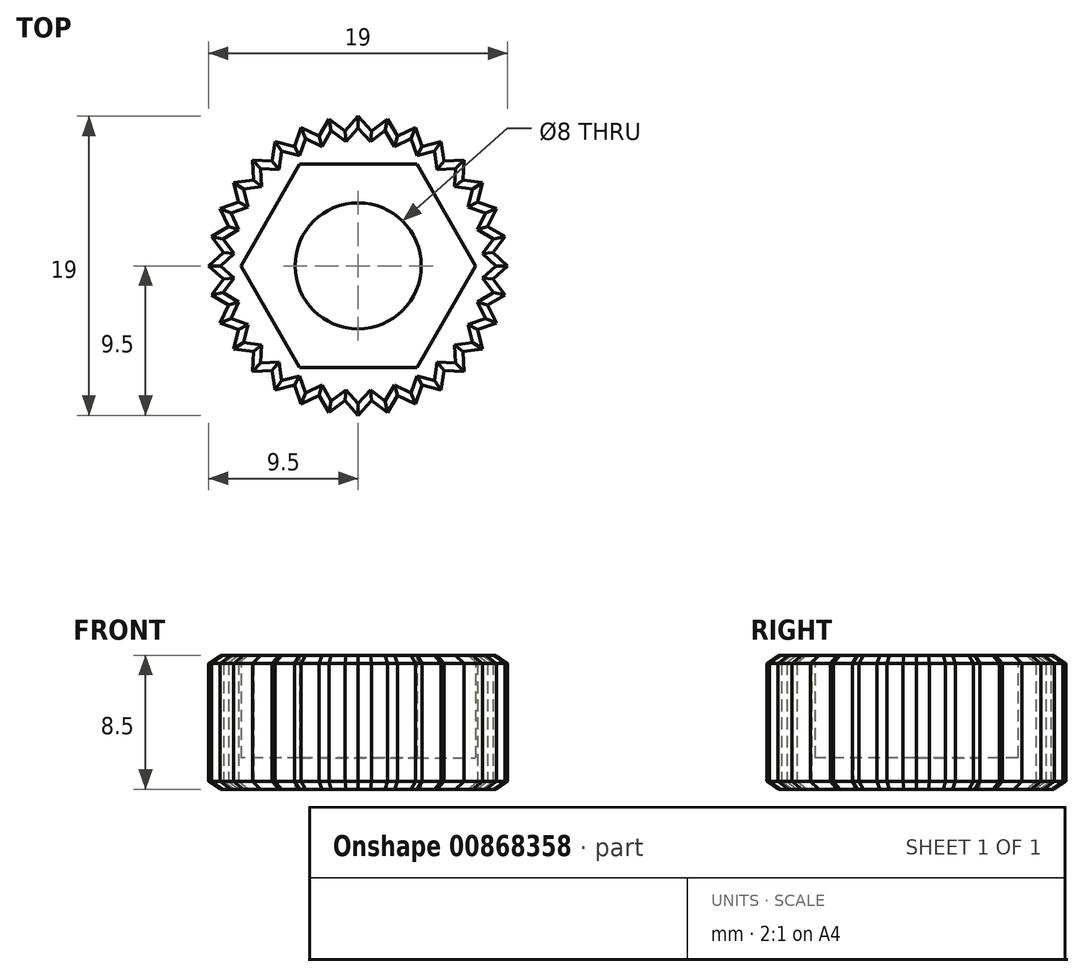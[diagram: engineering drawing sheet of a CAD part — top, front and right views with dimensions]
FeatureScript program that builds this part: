
annotation { "Feature Type Name" : "Feature", "Feature Type Description" : "" }
export const myFeature = defineFeature(function(context is Context, id is Id, definition is map)
    precondition{}
    {
        {
            var Q0;
            Q0=qCreatedBy(makeId("Top.planeOp"),FACE);
            var sketch = newSketch(context, id + "F0", { "sketchPlane" : qUnion([Q0])});
            skArc(sketch, "E0.cCircle", {"start": v(0, 6.45) * mm, "mid": v(-4.56, 4.56) * mm, "end": v(-6.45, 0) * mm, "construction": true});
            skLineSegment(sketch, "E0.4", {"start": v(-7.45, 0) * mm, "end": v(-3.72, 6.45) * mm});
            skLineSegment(sketch, "E0.5", {"start": v(-3.72, 6.45) * mm, "end": v(0, 6.45) * mm});
            skLineSegment(sketch, "E1", {"start": v(0, 12.28) * mm, "end": v(0, -11.98) * mm});
            skPoint(sketch, "E2", {"position": v(0, 9.5) * mm});
            skPoint(sketch, "E3", {"position": v(-9.5, 0) * mm});
            skCircle(sketch, "E4", {"center": v(0, 0) * mm, "radius": 8.6 * mm});
            skLineSegment(sketch, "E5", {"start": v(0, 9.5) * mm, "end": v(-0.84, 8.56) * mm});
            skLineSegment(sketch, "E6", {"start": v(-0.84, 8.56) * mm, "end": v(-1.85, 9.32) * mm});
            skLineSegment(sketch, "E7", {"start": v(-1.85, 9.32) * mm, "end": v(-2.5, 8.23) * mm});
            skLineSegment(sketch, "E8", {"start": v(-2.5, 8.23) * mm, "end": v(-3.64, 8.78) * mm});
            skLineSegment(sketch, "E9", {"start": v(-3.64, 8.78) * mm, "end": v(-4.05, 7.59) * mm});
            skLineSegment(sketch, "E10", {"start": v(-4.05, 7.59) * mm, "end": v(-5.28, 7.9) * mm});
            skLineSegment(sketch, "E11", {"start": v(-5.28, 7.9) * mm, "end": v(-5.46, 6.65) * mm});
            skLineSegment(sketch, "E12", {"start": v(-5.46, 6.65) * mm, "end": v(-6.72, 6.72) * mm});
            skLineSegment(sketch, "E13", {"start": v(-6.72, 6.72) * mm, "end": v(-6.65, 5.46) * mm});
            skLineSegment(sketch, "E14", {"start": v(-6.65, 5.46) * mm, "end": v(-7.9, 5.28) * mm});
            skLineSegment(sketch, "E15", {"start": v(-7.9, 5.28) * mm, "end": v(-7.58, 4.05) * mm});
            skLineSegment(sketch, "E16", {"start": v(-7.58, 4.05) * mm, "end": v(-8.78, 3.64) * mm});
            skLineSegment(sketch, "E17", {"start": v(-8.78, 3.64) * mm, "end": v(-8.23, 2.5) * mm});
            skLineSegment(sketch, "E18", {"start": v(-8.23, 2.5) * mm, "end": v(-9.32, 1.85) * mm});
            skLineSegment(sketch, "E19", {"start": v(-9.32, 1.85) * mm, "end": v(-8.56, 0.84) * mm});
            skLineSegment(sketch, "E20", {"start": v(-8.56, 0.84) * mm, "end": v(-9.5, 0) * mm});
            skLineSegment(sketch, "E21.MirrorCS", {"start": v(6.65, 5.46) * mm, "end": v(7.9, 5.28) * mm});
            skLineSegment(sketch, "E22.MirrorCS", {"start": v(8.56, 0.84) * mm, "end": v(9.5, 0) * mm});
            skLineSegment(sketch, "E23.MirrorCS", {"start": v(3.64, 8.78) * mm, "end": v(4.05, 7.59) * mm});
            skArc(sketch, "E24.MirrorCS", {"start": v(0, 6.45) * mm, "mid": v(4.56, 4.56) * mm, "end": v(6.45, 0) * mm, "construction": true});
            skLineSegment(sketch, "E25.MirrorCS", {"start": v(7.58, 4.05) * mm, "end": v(8.78, 3.64) * mm});
            skLineSegment(sketch, "E26.MirrorCS", {"start": v(4.05, 7.59) * mm, "end": v(5.28, 7.9) * mm});
            skLineSegment(sketch, "E27.MirrorCS", {"start": v(0.84, 8.56) * mm, "end": v(1.85, 9.32) * mm});
            skLineSegment(sketch, "E28.MirrorCS", {"start": v(8.23, 2.5) * mm, "end": v(9.32, 1.85) * mm});
            skLineSegment(sketch, "E29.MirrorCS", {"start": v(1.85, 9.32) * mm, "end": v(2.5, 8.23) * mm});
            skLineSegment(sketch, "E30.MirrorCS", {"start": v(0, 9.5) * mm, "end": v(0.84, 8.56) * mm});
            skLineSegment(sketch, "E31.MirrorCS", {"start": v(8.78, 3.64) * mm, "end": v(8.23, 2.5) * mm});
            skLineSegment(sketch, "E32.MirrorCS", {"start": v(2.5, 8.23) * mm, "end": v(3.64, 8.78) * mm});
            skLineSegment(sketch, "E33.MirrorCS", {"start": v(9.32, 1.85) * mm, "end": v(8.56, 0.84) * mm});
            skLineSegment(sketch, "E34.MirrorCS", {"start": v(5.28, 7.9) * mm, "end": v(5.46, 6.65) * mm});
            skLineSegment(sketch, "E35.MirrorCS", {"start": v(5.46, 6.65) * mm, "end": v(6.72, 6.72) * mm});
            skLineSegment(sketch, "E36.MirrorCS", {"start": v(3.72, 6.45) * mm, "end": v(0, 6.45) * mm});
            skLineSegment(sketch, "E37.MirrorCS", {"start": v(6.72, 6.72) * mm, "end": v(6.65, 5.46) * mm});
            skPoint(sketch, "E38.MirrorP", {"position": v(9.5, 0) * mm});
            skLineSegment(sketch, "E39.MirrorCS", {"start": v(7.45, 0) * mm, "end": v(3.72, 6.45) * mm});
            skLineSegment(sketch, "E40.MirrorCS", {"start": v(7.9, 5.28) * mm, "end": v(7.58, 4.05) * mm});
            skPoint(sketch, "E41.MirrorP", {"position": v(0, -9.5) * mm});
            skLineSegment(sketch, "E42.MirrorCS", {"start": v(1.85, -9.32) * mm, "end": v(2.5, -8.23) * mm});
            skLineSegment(sketch, "E43.MirrorCS", {"start": v(9.32, -1.85) * mm, "end": v(8.56, -0.84) * mm});
            skLineSegment(sketch, "E44.MirrorCS", {"start": v(0, -9.5) * mm, "end": v(-0.84, -8.56) * mm});
            skLineSegment(sketch, "E45.MirrorCS", {"start": v(-8.78, -3.64) * mm, "end": v(-8.23, -2.5) * mm});
            skLineSegment(sketch, "E46.MirrorCS", {"start": v(0.84, -8.56) * mm, "end": v(1.85, -9.32) * mm});
            skLineSegment(sketch, "E47.MirrorCS", {"start": v(5.28, -7.9) * mm, "end": v(5.46, -6.65) * mm});
            skLineSegment(sketch, "E48.MirrorCS", {"start": v(6.72, -6.72) * mm, "end": v(6.65, -5.46) * mm});
            skLineSegment(sketch, "E49.MirrorCS", {"start": v(-6.65, -5.46) * mm, "end": v(-7.9, -5.28) * mm});
            skLineSegment(sketch, "E50.MirrorCS", {"start": v(3.64, -8.78) * mm, "end": v(4.05, -7.59) * mm});
            skLineSegment(sketch, "E51.MirrorCS", {"start": v(-9.32, -1.85) * mm, "end": v(-8.56, -0.84) * mm});
            skLineSegment(sketch, "E52.MirrorCS", {"start": v(-5.28, -7.9) * mm, "end": v(-5.46, -6.65) * mm});
            skLineSegment(sketch, "E53.MirrorCS", {"start": v(5.46, -6.65) * mm, "end": v(6.72, -6.72) * mm});
            skLineSegment(sketch, "E54.MirrorCS", {"start": v(-7.9, -5.28) * mm, "end": v(-7.58, -4.05) * mm});
            skLineSegment(sketch, "E55.MirrorCS", {"start": v(-0.84, -8.56) * mm, "end": v(-1.85, -9.32) * mm});
            skLineSegment(sketch, "E56.MirrorCS", {"start": v(8.78, -3.64) * mm, "end": v(8.23, -2.5) * mm});
            skLineSegment(sketch, "E57.MirrorCS", {"start": v(2.5, -8.23) * mm, "end": v(3.64, -8.78) * mm});
            skLineSegment(sketch, "E58.MirrorCS", {"start": v(-7.58, -4.05) * mm, "end": v(-8.78, -3.64) * mm});
            skLineSegment(sketch, "E59.MirrorCS", {"start": v(-3.72, -6.45) * mm, "end": v(0, -6.45) * mm});
            skLineSegment(sketch, "E60.MirrorCS", {"start": v(-3.64, -8.78) * mm, "end": v(-4.05, -7.59) * mm});
            skLineSegment(sketch, "E61.MirrorCS", {"start": v(-8.23, -2.5) * mm, "end": v(-9.32, -1.85) * mm});
            skLineSegment(sketch, "E62.MirrorCS", {"start": v(4.05, -7.59) * mm, "end": v(5.28, -7.9) * mm});
            skLineSegment(sketch, "E63.MirrorCS", {"start": v(-4.05, -7.59) * mm, "end": v(-5.28, -7.9) * mm});
            skLineSegment(sketch, "E64.MirrorCS", {"start": v(6.65, -5.46) * mm, "end": v(7.9, -5.28) * mm});
            skLineSegment(sketch, "E65.MirrorCS", {"start": v(3.72, -6.45) * mm, "end": v(0, -6.45) * mm});
            skLineSegment(sketch, "E66.MirrorCS", {"start": v(-1.85, -9.32) * mm, "end": v(-2.5, -8.23) * mm});
            skLineSegment(sketch, "E67.MirrorCS", {"start": v(0, -9.5) * mm, "end": v(0.84, -8.56) * mm});
            skLineSegment(sketch, "E68.MirrorCS", {"start": v(-6.72, -6.72) * mm, "end": v(-6.65, -5.46) * mm});
            skLineSegment(sketch, "E69.MirrorCS", {"start": v(7.58, -4.05) * mm, "end": v(8.78, -3.64) * mm});
            skLineSegment(sketch, "E70.MirrorCS", {"start": v(7.9, -5.28) * mm, "end": v(7.58, -4.05) * mm});
            skLineSegment(sketch, "E71.MirrorCS", {"start": v(-2.5, -8.23) * mm, "end": v(-3.64, -8.78) * mm});
            skLineSegment(sketch, "E72.MirrorCS", {"start": v(8.23, -2.5) * mm, "end": v(9.32, -1.85) * mm});
            skLineSegment(sketch, "E73.MirrorCS", {"start": v(-5.46, -6.65) * mm, "end": v(-6.72, -6.72) * mm});
            skLineSegment(sketch, "E74", {"start": v(-8.56, -0.84) * mm, "end": v(-9.5, 0) * mm});
            skLineSegment(sketch, "E75", {"start": v(8.56, -0.84) * mm, "end": v(9.5, 0) * mm});
            skLineSegment(sketch, "E76", {"start": v(-7.45, 0) * mm, "end": v(-3.72, -6.45) * mm});
            skLineSegment(sketch, "E77", {"start": v(3.72, -6.45) * mm, "end": v(7.45, 0) * mm});
            skSolve(sketch);
        }
        {
            var Q0;
            Q0=makeQuery(id+"F0.imprint","IMPRINT",FACE,{"disambiguationData":[TD([[makeQuery(id+"F0.imprint","IMPRINT",EDGE,{"derivedFrom":sQuery(id+"F0.wireOp",EDGE,"E0.4")}),1.0]])]});
            var Q1;
            {var subQ16=sQuery(id+"F0.wireOp",EDGE,"E36.MirrorCS");Q1=makeQuery(id+"F0.imprint","IMPRINT",FACE,{"disambiguationData":[TD([[makeQuery(id+"F0.imprint","IMPRINT",EDGE,{"derivedFrom":subQ16}),-1.0]])]});}
            var Q2;
            Q2=makeQuery(id+"F0.imprint","IMPRINT",FACE,{"disambiguationData":[TD([[makeQuery(id+"F0.imprint","IMPRINT",EDGE,{"derivedFrom":sQuery(id+"F0.wireOp",EDGE,"E0.4")}),-1.0]])]});
            var Q3;
            {var subQ1=sQuery(id+"F0.wireOp",EDGE,"E36.MirrorCS");Q3=makeQuery(id+"F0.imprint","IMPRINT",FACE,{"disambiguationData":[TD([[makeQuery(id+"F0.imprint","IMPRINT",EDGE,{"derivedFrom":subQ1}),1.0]])]});}
            var Q4;
            {var subQ0=sQuery(id+"F0.wireOp",EDGE,"E6");Q4=makeQuery(id+"F0.imprint","IMPRINT",FACE,{"disambiguationData":[TD([[makeQuery(id+"F0.imprint","IMPRINT",EDGE,{"derivedFrom":subQ0}),1.0]])]});}
            var Q5;
            {var subQ0=sQuery(id+"F0.wireOp",EDGE,"E8");Q5=makeQuery(id+"F0.imprint","IMPRINT",FACE,{"disambiguationData":[TD([[makeQuery(id+"F0.imprint","IMPRINT",EDGE,{"derivedFrom":subQ0}),1.0]])]});}
            var Q6;
            {var subQ0=sQuery(id+"F0.wireOp",EDGE,"E30.MirrorCS");Q6=makeQuery(id+"F0.imprint","IMPRINT",FACE,{"disambiguationData":[TD([[makeQuery(id+"F0.imprint","IMPRINT",EDGE,{"derivedFrom":subQ0}),-1.0]])]});}
            var Q7;
            {var subQ0=sQuery(id+"F0.wireOp",EDGE,"E25.MirrorCS");Q7=makeQuery(id+"F0.imprint","IMPRINT",FACE,{"disambiguationData":[TD([[makeQuery(id+"F0.imprint","IMPRINT",EDGE,{"derivedFrom":subQ0}),-1.0]])]});}
            var Q8;
            {var subQ0=sQuery(id+"F0.wireOp",EDGE,"E26.MirrorCS");Q8=makeQuery(id+"F0.imprint","IMPRINT",FACE,{"disambiguationData":[TD([[makeQuery(id+"F0.imprint","IMPRINT",EDGE,{"derivedFrom":subQ0}),-1.0]])]});}
            var Q9;
            {var subQ0=sQuery(id+"F0.wireOp",EDGE,"E64.MirrorCS");Q9=makeQuery(id+"F0.imprint","IMPRINT",FACE,{"disambiguationData":[TD([[makeQuery(id+"F0.imprint","IMPRINT",EDGE,{"derivedFrom":subQ0}),1.0]])]});}
            var Q10;
            {var subQ0=sQuery(id+"F0.wireOp",EDGE,"E5");Q10=makeQuery(id+"F0.imprint","IMPRINT",FACE,{"disambiguationData":[TD([[makeQuery(id+"F0.imprint","IMPRINT",EDGE,{"derivedFrom":subQ0}),1.0]])]});}
            var Q11;
            {var subQ0=sQuery(id+"F0.wireOp",EDGE,"E67.MirrorCS");Q11=makeQuery(id+"F0.imprint","IMPRINT",FACE,{"disambiguationData":[TD([[makeQuery(id+"F0.imprint","IMPRINT",EDGE,{"derivedFrom":subQ0}),1.0]])]});}
            var Q12;
            {var subQ0=sQuery(id+"F0.wireOp",EDGE,"E52.MirrorCS");Q12=makeQuery(id+"F0.imprint","IMPRINT",FACE,{"disambiguationData":[TD([[makeQuery(id+"F0.imprint","IMPRINT",EDGE,{"derivedFrom":subQ0}),-1.0]])]});}
            var Q13;
            {var subQ0=sQuery(id+"F0.wireOp",EDGE,"E10");Q13=makeQuery(id+"F0.imprint","IMPRINT",FACE,{"disambiguationData":[TD([[makeQuery(id+"F0.imprint","IMPRINT",EDGE,{"derivedFrom":subQ0}),1.0]])]});}
            var Q14;
            {var subQ2=sQuery(id+"F0.wireOp",EDGE,"E50.MirrorCS");Q14=makeQuery(id+"F0.imprint","IMPRINT",FACE,{"disambiguationData":[TD([[makeQuery(id+"F0.imprint","IMPRINT",EDGE,{"derivedFrom":subQ2}),1.0]])]});}
            var Q15;
            {var subQ0=sQuery(id+"F0.wireOp",EDGE,"E14");Q15=makeQuery(id+"F0.imprint","IMPRINT",FACE,{"disambiguationData":[TD([[makeQuery(id+"F0.imprint","IMPRINT",EDGE,{"derivedFrom":subQ0}),1.0]])]});}
            var Q16;
            {var subQ0=sQuery(id+"F0.wireOp",EDGE,"E18");Q16=makeQuery(id+"F0.imprint","IMPRINT",FACE,{"disambiguationData":[TD([[makeQuery(id+"F0.imprint","IMPRINT",EDGE,{"derivedFrom":subQ0}),1.0]])]});}
            var Q17;
            {var subQ0=sQuery(id+"F0.wireOp",EDGE,"E16");Q17=makeQuery(id+"F0.imprint","IMPRINT",FACE,{"disambiguationData":[TD([[makeQuery(id+"F0.imprint","IMPRINT",EDGE,{"derivedFrom":subQ0}),1.0]])]});}
            var Q18;
            {var subQ2=sQuery(id+"F0.wireOp",EDGE,"E51.MirrorCS");Q18=makeQuery(id+"F0.imprint","IMPRINT",FACE,{"disambiguationData":[TD([[makeQuery(id+"F0.imprint","IMPRINT",EDGE,{"derivedFrom":subQ2}),-1.0]])]});}
            var Q19;
            {var subQ0=sQuery(id+"F0.wireOp",EDGE,"E27.MirrorCS");Q19=makeQuery(id+"F0.imprint","IMPRINT",FACE,{"disambiguationData":[TD([[makeQuery(id+"F0.imprint","IMPRINT",EDGE,{"derivedFrom":subQ0}),-1.0]])]});}
            var Q20;
            {var subQ0=sQuery(id+"F0.wireOp",EDGE,"E42.MirrorCS");Q20=makeQuery(id+"F0.imprint","IMPRINT",FACE,{"disambiguationData":[TD([[makeQuery(id+"F0.imprint","IMPRINT",EDGE,{"derivedFrom":subQ0}),1.0]])]});}
            var Q21;
            {var subQ0=sQuery(id+"F0.wireOp",EDGE,"E20");Q21=makeQuery(id+"F0.imprint","IMPRINT",FACE,{"disambiguationData":[TD([[makeQuery(id+"F0.imprint","IMPRINT",EDGE,{"derivedFrom":subQ0}),1.0]])]});}
            var Q22;
            {var subQ0=sQuery(id+"F0.wireOp",EDGE,"E23.MirrorCS");Q22=makeQuery(id+"F0.imprint","IMPRINT",FACE,{"disambiguationData":[TD([[makeQuery(id+"F0.imprint","IMPRINT",EDGE,{"derivedFrom":subQ0}),-1.0]])]});}
            var Q23;
            {var subQ0=sQuery(id+"F0.wireOp",EDGE,"E49.MirrorCS");Q23=makeQuery(id+"F0.imprint","IMPRINT",FACE,{"disambiguationData":[TD([[makeQuery(id+"F0.imprint","IMPRINT",EDGE,{"derivedFrom":subQ0}),-1.0]])]});}
            var Q24;
            {var subQ0=sQuery(id+"F0.wireOp",EDGE,"E47.MirrorCS");Q24=makeQuery(id+"F0.imprint","IMPRINT",FACE,{"disambiguationData":[TD([[makeQuery(id+"F0.imprint","IMPRINT",EDGE,{"derivedFrom":subQ0}),1.0]])]});}
            var Q25;
            {var subQ0=sQuery(id+"F0.wireOp",EDGE,"E22.MirrorCS");Q25=makeQuery(id+"F0.imprint","IMPRINT",FACE,{"disambiguationData":[TD([[makeQuery(id+"F0.imprint","IMPRINT",EDGE,{"derivedFrom":subQ0}),-1.0]])]});}
            var Q26;
            {var subQ0=sQuery(id+"F0.wireOp",EDGE,"E28.MirrorCS");Q26=makeQuery(id+"F0.imprint","IMPRINT",FACE,{"disambiguationData":[TD([[makeQuery(id+"F0.imprint","IMPRINT",EDGE,{"derivedFrom":subQ0}),-1.0]])]});}
            var Q27;
            {var subQ0=sQuery(id+"F0.wireOp",EDGE,"E35.MirrorCS");Q27=makeQuery(id+"F0.imprint","IMPRINT",FACE,{"disambiguationData":[TD([[makeQuery(id+"F0.imprint","IMPRINT",EDGE,{"derivedFrom":subQ0}),-1.0]])]});}
            var Q28;
            {var subQ0=sQuery(id+"F0.wireOp",EDGE,"E43.MirrorCS");Q28=makeQuery(id+"F0.imprint","IMPRINT",FACE,{"disambiguationData":[TD([[makeQuery(id+"F0.imprint","IMPRINT",EDGE,{"derivedFrom":subQ0}),1.0]])]});}
            var Q29;
            {var subQ0=sQuery(id+"F0.wireOp",EDGE,"E68.MirrorCS");Q29=makeQuery(id+"F0.imprint","IMPRINT",FACE,{"disambiguationData":[TD([[makeQuery(id+"F0.imprint","IMPRINT",EDGE,{"derivedFrom":subQ0}),-1.0]])]});}
            var Q30;
            {var subQ0=sQuery(id+"F0.wireOp",EDGE,"E56.MirrorCS");Q30=makeQuery(id+"F0.imprint","IMPRINT",FACE,{"disambiguationData":[TD([[makeQuery(id+"F0.imprint","IMPRINT",EDGE,{"derivedFrom":subQ0}),1.0]])]});}
            var Q31;
            {var subQ0=sQuery(id+"F0.wireOp",EDGE,"E44.MirrorCS");Q31=makeQuery(id+"F0.imprint","IMPRINT",FACE,{"disambiguationData":[TD([[makeQuery(id+"F0.imprint","IMPRINT",EDGE,{"derivedFrom":subQ0}),-1.0]])]});}
            var Q32;
            {var subQ0=sQuery(id+"F0.wireOp",EDGE,"E45.MirrorCS");Q32=makeQuery(id+"F0.imprint","IMPRINT",FACE,{"disambiguationData":[TD([[makeQuery(id+"F0.imprint","IMPRINT",EDGE,{"derivedFrom":subQ0}),-1.0]])]});}
            var Q33;
            {var subQ0=sQuery(id+"F0.wireOp",EDGE,"E12");Q33=makeQuery(id+"F0.imprint","IMPRINT",FACE,{"disambiguationData":[TD([[makeQuery(id+"F0.imprint","IMPRINT",EDGE,{"derivedFrom":subQ0}),1.0]])]});}
            var Q34;
            {var subQ0=sQuery(id+"F0.wireOp",EDGE,"E60.MirrorCS");Q34=makeQuery(id+"F0.imprint","IMPRINT",FACE,{"disambiguationData":[TD([[makeQuery(id+"F0.imprint","IMPRINT",EDGE,{"derivedFrom":subQ0}),-1.0]])]});}
            var Q35;
            {var subQ0=sQuery(id+"F0.wireOp",EDGE,"E21.MirrorCS");Q35=makeQuery(id+"F0.imprint","IMPRINT",FACE,{"disambiguationData":[TD([[makeQuery(id+"F0.imprint","IMPRINT",EDGE,{"derivedFrom":subQ0}),-1.0]])]});}
            var Q36;
            {var subQ2=sQuery(id+"F0.wireOp",EDGE,"E48.MirrorCS");Q36=makeQuery(id+"F0.imprint","IMPRINT",FACE,{"disambiguationData":[TD([[makeQuery(id+"F0.imprint","IMPRINT",EDGE,{"derivedFrom":subQ2}),1.0]])]});}
            var Q37;
            {var subQ0=sQuery(id+"F0.wireOp",EDGE,"E55.MirrorCS");Q37=makeQuery(id+"F0.imprint","IMPRINT",FACE,{"disambiguationData":[TD([[makeQuery(id+"F0.imprint","IMPRINT",EDGE,{"derivedFrom":subQ0}),-1.0]])]});}
            extrude(context, id + "F1", {"entities" : qUnion([Q0, Q1, Q2, Q3, Q4, Q5, Q6, Q7, Q8, Q9, Q10, Q11, Q12, Q13, Q14, Q15, Q16, Q17, Q18, Q19, Q20, Q21, Q22, Q23, Q24, Q25, Q26, Q27, Q28, Q29, Q30, Q31, Q32, Q33, Q34, Q35, Q36, Q37]), "depth" : 2 * mm, "offsetDistance" : 25 * mm});
        }
        {
            var Q0;
            {var subQ16=sQuery(id+"F0.wireOp",EDGE,"E36.MirrorCS");Q0=makeQuery(id+"F0.imprint","IMPRINT",FACE,{"disambiguationData":[TD([[makeQuery(id+"F0.imprint","IMPRINT",EDGE,{"derivedFrom":subQ16}),-1.0]])]});}
            var Q1;
            Q1=makeQuery(id+"F0.imprint","IMPRINT",FACE,{"disambiguationData":[TD([[makeQuery(id+"F0.imprint","IMPRINT",EDGE,{"derivedFrom":sQuery(id+"F0.wireOp",EDGE,"E0.4")}),1.0]])]});
            var Q2;
            {var subQ0=sQuery(id+"F0.wireOp",EDGE,"E47.MirrorCS");Q2=makeQuery(id+"F0.imprint","IMPRINT",FACE,{"disambiguationData":[TD([[makeQuery(id+"F0.imprint","IMPRINT",EDGE,{"derivedFrom":subQ0}),1.0]])]});}
            var Q3;
            {var subQ2=sQuery(id+"F0.wireOp",EDGE,"E48.MirrorCS");Q3=makeQuery(id+"F0.imprint","IMPRINT",FACE,{"disambiguationData":[TD([[makeQuery(id+"F0.imprint","IMPRINT",EDGE,{"derivedFrom":subQ2}),1.0]])]});}
            var Q4;
            {var subQ0=sQuery(id+"F0.wireOp",EDGE,"E64.MirrorCS");Q4=makeQuery(id+"F0.imprint","IMPRINT",FACE,{"disambiguationData":[TD([[makeQuery(id+"F0.imprint","IMPRINT",EDGE,{"derivedFrom":subQ0}),1.0]])]});}
            var Q5;
            {var subQ0=sQuery(id+"F0.wireOp",EDGE,"E56.MirrorCS");Q5=makeQuery(id+"F0.imprint","IMPRINT",FACE,{"disambiguationData":[TD([[makeQuery(id+"F0.imprint","IMPRINT",EDGE,{"derivedFrom":subQ0}),1.0]])]});}
            var Q6;
            {var subQ0=sQuery(id+"F0.wireOp",EDGE,"E43.MirrorCS");Q6=makeQuery(id+"F0.imprint","IMPRINT",FACE,{"disambiguationData":[TD([[makeQuery(id+"F0.imprint","IMPRINT",EDGE,{"derivedFrom":subQ0}),1.0]])]});}
            var Q7;
            {var subQ0=sQuery(id+"F0.wireOp",EDGE,"E22.MirrorCS");Q7=makeQuery(id+"F0.imprint","IMPRINT",FACE,{"disambiguationData":[TD([[makeQuery(id+"F0.imprint","IMPRINT",EDGE,{"derivedFrom":subQ0}),-1.0]])]});}
            var Q8;
            {var subQ0=sQuery(id+"F0.wireOp",EDGE,"E28.MirrorCS");Q8=makeQuery(id+"F0.imprint","IMPRINT",FACE,{"disambiguationData":[TD([[makeQuery(id+"F0.imprint","IMPRINT",EDGE,{"derivedFrom":subQ0}),-1.0]])]});}
            var Q9;
            {var subQ0=sQuery(id+"F0.wireOp",EDGE,"E25.MirrorCS");Q9=makeQuery(id+"F0.imprint","IMPRINT",FACE,{"disambiguationData":[TD([[makeQuery(id+"F0.imprint","IMPRINT",EDGE,{"derivedFrom":subQ0}),-1.0]])]});}
            var Q10;
            {var subQ0=sQuery(id+"F0.wireOp",EDGE,"E21.MirrorCS");Q10=makeQuery(id+"F0.imprint","IMPRINT",FACE,{"disambiguationData":[TD([[makeQuery(id+"F0.imprint","IMPRINT",EDGE,{"derivedFrom":subQ0}),-1.0]])]});}
            var Q11;
            {var subQ0=sQuery(id+"F0.wireOp",EDGE,"E35.MirrorCS");Q11=makeQuery(id+"F0.imprint","IMPRINT",FACE,{"disambiguationData":[TD([[makeQuery(id+"F0.imprint","IMPRINT",EDGE,{"derivedFrom":subQ0}),-1.0]])]});}
            var Q12;
            {var subQ0=sQuery(id+"F0.wireOp",EDGE,"E26.MirrorCS");Q12=makeQuery(id+"F0.imprint","IMPRINT",FACE,{"disambiguationData":[TD([[makeQuery(id+"F0.imprint","IMPRINT",EDGE,{"derivedFrom":subQ0}),-1.0]])]});}
            var Q13;
            {var subQ0=sQuery(id+"F0.wireOp",EDGE,"E23.MirrorCS");Q13=makeQuery(id+"F0.imprint","IMPRINT",FACE,{"disambiguationData":[TD([[makeQuery(id+"F0.imprint","IMPRINT",EDGE,{"derivedFrom":subQ0}),-1.0]])]});}
            var Q14;
            {var subQ2=sQuery(id+"F0.wireOp",EDGE,"E50.MirrorCS");Q14=makeQuery(id+"F0.imprint","IMPRINT",FACE,{"disambiguationData":[TD([[makeQuery(id+"F0.imprint","IMPRINT",EDGE,{"derivedFrom":subQ2}),1.0]])]});}
            var Q15;
            {var subQ0=sQuery(id+"F0.wireOp",EDGE,"E42.MirrorCS");Q15=makeQuery(id+"F0.imprint","IMPRINT",FACE,{"disambiguationData":[TD([[makeQuery(id+"F0.imprint","IMPRINT",EDGE,{"derivedFrom":subQ0}),1.0]])]});}
            var Q16;
            {var subQ0=sQuery(id+"F0.wireOp",EDGE,"E67.MirrorCS");Q16=makeQuery(id+"F0.imprint","IMPRINT",FACE,{"disambiguationData":[TD([[makeQuery(id+"F0.imprint","IMPRINT",EDGE,{"derivedFrom":subQ0}),1.0]])]});}
            var Q17;
            {var subQ0=sQuery(id+"F0.wireOp",EDGE,"E44.MirrorCS");Q17=makeQuery(id+"F0.imprint","IMPRINT",FACE,{"disambiguationData":[TD([[makeQuery(id+"F0.imprint","IMPRINT",EDGE,{"derivedFrom":subQ0}),-1.0]])]});}
            var Q18;
            {var subQ0=sQuery(id+"F0.wireOp",EDGE,"E55.MirrorCS");Q18=makeQuery(id+"F0.imprint","IMPRINT",FACE,{"disambiguationData":[TD([[makeQuery(id+"F0.imprint","IMPRINT",EDGE,{"derivedFrom":subQ0}),-1.0]])]});}
            var Q19;
            {var subQ0=sQuery(id+"F0.wireOp",EDGE,"E60.MirrorCS");Q19=makeQuery(id+"F0.imprint","IMPRINT",FACE,{"disambiguationData":[TD([[makeQuery(id+"F0.imprint","IMPRINT",EDGE,{"derivedFrom":subQ0}),-1.0]])]});}
            var Q20;
            {var subQ0=sQuery(id+"F0.wireOp",EDGE,"E52.MirrorCS");Q20=makeQuery(id+"F0.imprint","IMPRINT",FACE,{"disambiguationData":[TD([[makeQuery(id+"F0.imprint","IMPRINT",EDGE,{"derivedFrom":subQ0}),-1.0]])]});}
            var Q21;
            {var subQ0=sQuery(id+"F0.wireOp",EDGE,"E6");Q21=makeQuery(id+"F0.imprint","IMPRINT",FACE,{"disambiguationData":[TD([[makeQuery(id+"F0.imprint","IMPRINT",EDGE,{"derivedFrom":subQ0}),1.0]])]});}
            var Q22;
            {var subQ0=sQuery(id+"F0.wireOp",EDGE,"E27.MirrorCS");Q22=makeQuery(id+"F0.imprint","IMPRINT",FACE,{"disambiguationData":[TD([[makeQuery(id+"F0.imprint","IMPRINT",EDGE,{"derivedFrom":subQ0}),-1.0]])]});}
            var Q23;
            {var subQ0=sQuery(id+"F0.wireOp",EDGE,"E30.MirrorCS");Q23=makeQuery(id+"F0.imprint","IMPRINT",FACE,{"disambiguationData":[TD([[makeQuery(id+"F0.imprint","IMPRINT",EDGE,{"derivedFrom":subQ0}),-1.0]])]});}
            var Q24;
            {var subQ0=sQuery(id+"F0.wireOp",EDGE,"E5");Q24=makeQuery(id+"F0.imprint","IMPRINT",FACE,{"disambiguationData":[TD([[makeQuery(id+"F0.imprint","IMPRINT",EDGE,{"derivedFrom":subQ0}),1.0]])]});}
            var Q25;
            {var subQ0=sQuery(id+"F0.wireOp",EDGE,"E68.MirrorCS");Q25=makeQuery(id+"F0.imprint","IMPRINT",FACE,{"disambiguationData":[TD([[makeQuery(id+"F0.imprint","IMPRINT",EDGE,{"derivedFrom":subQ0}),-1.0]])]});}
            var Q26;
            {var subQ0=sQuery(id+"F0.wireOp",EDGE,"E49.MirrorCS");Q26=makeQuery(id+"F0.imprint","IMPRINT",FACE,{"disambiguationData":[TD([[makeQuery(id+"F0.imprint","IMPRINT",EDGE,{"derivedFrom":subQ0}),-1.0]])]});}
            var Q27;
            {var subQ0=sQuery(id+"F0.wireOp",EDGE,"E45.MirrorCS");Q27=makeQuery(id+"F0.imprint","IMPRINT",FACE,{"disambiguationData":[TD([[makeQuery(id+"F0.imprint","IMPRINT",EDGE,{"derivedFrom":subQ0}),-1.0]])]});}
            var Q28;
            {var subQ2=sQuery(id+"F0.wireOp",EDGE,"E51.MirrorCS");Q28=makeQuery(id+"F0.imprint","IMPRINT",FACE,{"disambiguationData":[TD([[makeQuery(id+"F0.imprint","IMPRINT",EDGE,{"derivedFrom":subQ2}),-1.0]])]});}
            var Q29;
            {var subQ0=sQuery(id+"F0.wireOp",EDGE,"E20");Q29=makeQuery(id+"F0.imprint","IMPRINT",FACE,{"disambiguationData":[TD([[makeQuery(id+"F0.imprint","IMPRINT",EDGE,{"derivedFrom":subQ0}),1.0]])]});}
            var Q30;
            {var subQ0=sQuery(id+"F0.wireOp",EDGE,"E18");Q30=makeQuery(id+"F0.imprint","IMPRINT",FACE,{"disambiguationData":[TD([[makeQuery(id+"F0.imprint","IMPRINT",EDGE,{"derivedFrom":subQ0}),1.0]])]});}
            var Q31;
            {var subQ0=sQuery(id+"F0.wireOp",EDGE,"E16");Q31=makeQuery(id+"F0.imprint","IMPRINT",FACE,{"disambiguationData":[TD([[makeQuery(id+"F0.imprint","IMPRINT",EDGE,{"derivedFrom":subQ0}),1.0]])]});}
            var Q32;
            {var subQ0=sQuery(id+"F0.wireOp",EDGE,"E14");Q32=makeQuery(id+"F0.imprint","IMPRINT",FACE,{"disambiguationData":[TD([[makeQuery(id+"F0.imprint","IMPRINT",EDGE,{"derivedFrom":subQ0}),1.0]])]});}
            var Q33;
            {var subQ0=sQuery(id+"F0.wireOp",EDGE,"E12");Q33=makeQuery(id+"F0.imprint","IMPRINT",FACE,{"disambiguationData":[TD([[makeQuery(id+"F0.imprint","IMPRINT",EDGE,{"derivedFrom":subQ0}),1.0]])]});}
            var Q34;
            {var subQ0=sQuery(id+"F0.wireOp",EDGE,"E10");Q34=makeQuery(id+"F0.imprint","IMPRINT",FACE,{"disambiguationData":[TD([[makeQuery(id+"F0.imprint","IMPRINT",EDGE,{"derivedFrom":subQ0}),1.0]])]});}
            var Q35;
            {var subQ0=sQuery(id+"F0.wireOp",EDGE,"E8");Q35=makeQuery(id+"F0.imprint","IMPRINT",FACE,{"disambiguationData":[TD([[makeQuery(id+"F0.imprint","IMPRINT",EDGE,{"derivedFrom":subQ0}),1.0]])]});}
            extrude(context, id + "F2", {"entities" : qUnion([Q0, Q1, Q2, Q3, Q4, Q5, Q6, Q7, Q8, Q9, Q10, Q11, Q12, Q13, Q14, Q15, Q16, Q17, Q18, Q19, Q20, Q21, Q22, Q23, Q24, Q25, Q26, Q27, Q28, Q29, Q30, Q31, Q32, Q33, Q34, Q35]), "operationType" : NewBodyOperationType.ADD, "depth" : 8.5 * mm, "offsetDistance" : 25 * mm});
        }
        {
            var Q0;
            Q0=makeQuery(id+"F1.opExtrude","CAP_FACE",FACE,{"disambiguationData":[OSD([sQuery(id+"F0.wireOp",EDGE,"E5"),sQuery(id+"F0.wireOp",EDGE,"E6"),sQuery(id+"F0.wireOp",EDGE,"E7"),sQuery(id+"F0.wireOp",EDGE,"E8"),sQuery(id+"F0.wireOp",EDGE,"E9"),sQuery(id+"F0.wireOp",EDGE,"E10"),sQuery(id+"F0.wireOp",EDGE,"E11"),sQuery(id+"F0.wireOp",EDGE,"E12"),sQuery(id+"F0.wireOp",EDGE,"E13"),sQuery(id+"F0.wireOp",EDGE,"E14"),sQuery(id+"F0.wireOp",EDGE,"E15"),sQuery(id+"F0.wireOp",EDGE,"E16"),sQuery(id+"F0.wireOp",EDGE,"E17"),sQuery(id+"F0.wireOp",EDGE,"E18"),sQuery(id+"F0.wireOp",EDGE,"E19"),sQuery(id+"F0.wireOp",EDGE,"E20"),sQuery(id+"F0.wireOp",EDGE,"E21.MirrorCS"),sQuery(id+"F0.wireOp",EDGE,"E22.MirrorCS"),sQuery(id+"F0.wireOp",EDGE,"E23.MirrorCS"),sQuery(id+"F0.wireOp",EDGE,"E25.MirrorCS"),sQuery(id+"F0.wireOp",EDGE,"E26.MirrorCS"),sQuery(id+"F0.wireOp",EDGE,"E27.MirrorCS"),sQuery(id+"F0.wireOp",EDGE,"E28.MirrorCS"),sQuery(id+"F0.wireOp",EDGE,"E29.MirrorCS"),sQuery(id+"F0.wireOp",EDGE,"E30.MirrorCS"),sQuery(id+"F0.wireOp",EDGE,"E31.MirrorCS"),sQuery(id+"F0.wireOp",EDGE,"E32.MirrorCS"),sQuery(id+"F0.wireOp",EDGE,"E33.MirrorCS"),sQuery(id+"F0.wireOp",EDGE,"E34.MirrorCS"),sQuery(id+"F0.wireOp",EDGE,"E35.MirrorCS"),sQuery(id+"F0.wireOp",EDGE,"E37.MirrorCS"),sQuery(id+"F0.wireOp",EDGE,"E40.MirrorCS"),sQuery(id+"F0.wireOp",EDGE,"E42.MirrorCS"),sQuery(id+"F0.wireOp",EDGE,"E43.MirrorCS"),sQuery(id+"F0.wireOp",EDGE,"E44.MirrorCS"),sQuery(id+"F0.wireOp",EDGE,"E45.MirrorCS"),sQuery(id+"F0.wireOp",EDGE,"E46.MirrorCS"),sQuery(id+"F0.wireOp",EDGE,"E47.MirrorCS"),sQuery(id+"F0.wireOp",EDGE,"E48.MirrorCS"),sQuery(id+"F0.wireOp",EDGE,"E49.MirrorCS"),sQuery(id+"F0.wireOp",EDGE,"E50.MirrorCS"),sQuery(id+"F0.wireOp",EDGE,"E51.MirrorCS"),sQuery(id+"F0.wireOp",EDGE,"E52.MirrorCS"),sQuery(id+"F0.wireOp",EDGE,"E53.MirrorCS"),sQuery(id+"F0.wireOp",EDGE,"E54.MirrorCS"),sQuery(id+"F0.wireOp",EDGE,"E55.MirrorCS"),sQuery(id+"F0.wireOp",EDGE,"E56.MirrorCS"),sQuery(id+"F0.wireOp",EDGE,"E57.MirrorCS"),sQuery(id+"F0.wireOp",EDGE,"E58.MirrorCS"),sQuery(id+"F0.wireOp",EDGE,"E60.MirrorCS"),sQuery(id+"F0.wireOp",EDGE,"E61.MirrorCS"),sQuery(id+"F0.wireOp",EDGE,"E62.MirrorCS"),sQuery(id+"F0.wireOp",EDGE,"E63.MirrorCS"),sQuery(id+"F0.wireOp",EDGE,"E64.MirrorCS"),sQuery(id+"F0.wireOp",EDGE,"E66.MirrorCS"),sQuery(id+"F0.wireOp",EDGE,"E67.MirrorCS"),sQuery(id+"F0.wireOp",EDGE,"E68.MirrorCS"),sQuery(id+"F0.wireOp",EDGE,"E69.MirrorCS"),sQuery(id+"F0.wireOp",EDGE,"E70.MirrorCS"),sQuery(id+"F0.wireOp",EDGE,"E71.MirrorCS"),sQuery(id+"F0.wireOp",EDGE,"E72.MirrorCS"),sQuery(id+"F0.wireOp",EDGE,"E73.MirrorCS"),sQuery(id+"F0.wireOp",EDGE,"E74"),sQuery(id+"F0.wireOp",EDGE,"E75")])],"isStart":true});
            chamfer(context, id + "F3", {"entities" : qUnion([Q0]), "width" : 0.5 * mm, "tangentPropagation" : true});
        }
        {
            var Q0;
            Q0=makeQuery(id+"F2.opExtrude","CAP_EDGE",EDGE,{"disambiguationData":[OSD([sQuery(id+"F0.wireOp",EDGE,"E60.MirrorCS")])],"isStart":false});
            var Q1;
            Q1=makeQuery(id+"F2.opExtrude","CAP_EDGE",EDGE,{"disambiguationData":[OSD([sQuery(id+"F0.wireOp",EDGE,"E71.MirrorCS")])],"isStart":false});
            var Q2;
            Q2=makeQuery(id+"F2.opExtrude","CAP_EDGE",EDGE,{"disambiguationData":[OSD([sQuery(id+"F0.wireOp",EDGE,"E66.MirrorCS")])],"isStart":false});
            var Q3;
            Q3=makeQuery(id+"F2.opExtrude","CAP_EDGE",EDGE,{"disambiguationData":[OSD([sQuery(id+"F0.wireOp",EDGE,"E55.MirrorCS")])],"isStart":false});
            var Q4;
            Q4=makeQuery(id+"F2.opExtrude","CAP_EDGE",EDGE,{"disambiguationData":[OSD([sQuery(id+"F0.wireOp",EDGE,"E44.MirrorCS")])],"isStart":false});
            var Q5;
            Q5=makeQuery(id+"F2.opExtrude","CAP_EDGE",EDGE,{"disambiguationData":[OSD([sQuery(id+"F0.wireOp",EDGE,"E67.MirrorCS")])],"isStart":false});
            var Q6;
            Q6=makeQuery(id+"F2.opExtrude","CAP_EDGE",EDGE,{"disambiguationData":[OSD([sQuery(id+"F0.wireOp",EDGE,"E46.MirrorCS")])],"isStart":false});
            var Q7;
            Q7=makeQuery(id+"F2.opExtrude","CAP_EDGE",EDGE,{"disambiguationData":[OSD([sQuery(id+"F0.wireOp",EDGE,"E42.MirrorCS")])],"isStart":false});
            var Q8;
            Q8=makeQuery(id+"F2.opExtrude","CAP_EDGE",EDGE,{"disambiguationData":[OSD([sQuery(id+"F0.wireOp",EDGE,"E57.MirrorCS")])],"isStart":false});
            var Q9;
            Q9=makeQuery(id+"F2.opExtrude","CAP_EDGE",EDGE,{"disambiguationData":[OSD([sQuery(id+"F0.wireOp",EDGE,"E50.MirrorCS")])],"isStart":false});
            var Q10;
            Q10=makeQuery(id+"F2.opExtrude","CAP_EDGE",EDGE,{"disambiguationData":[OSD([sQuery(id+"F0.wireOp",EDGE,"E62.MirrorCS")])],"isStart":false});
            var Q11;
            Q11=makeQuery(id+"F2.opExtrude","CAP_EDGE",EDGE,{"disambiguationData":[OSD([sQuery(id+"F0.wireOp",EDGE,"E47.MirrorCS")])],"isStart":false});
            var Q12;
            Q12=makeQuery(id+"F2.opExtrude","CAP_EDGE",EDGE,{"disambiguationData":[OSD([sQuery(id+"F0.wireOp",EDGE,"E53.MirrorCS")])],"isStart":false});
            var Q13;
            Q13=makeQuery(id+"F2.opExtrude","CAP_EDGE",EDGE,{"disambiguationData":[OSD([sQuery(id+"F0.wireOp",EDGE,"E48.MirrorCS")])],"isStart":false});
            var Q14;
            Q14=makeQuery(id+"F2.opExtrude","CAP_EDGE",EDGE,{"disambiguationData":[OSD([sQuery(id+"F0.wireOp",EDGE,"E64.MirrorCS")])],"isStart":false});
            var Q15;
            Q15=makeQuery(id+"F2.opExtrude","CAP_EDGE",EDGE,{"disambiguationData":[OSD([sQuery(id+"F0.wireOp",EDGE,"E70.MirrorCS")])],"isStart":false});
            var Q16;
            Q16=makeQuery(id+"F2.opExtrude","CAP_EDGE",EDGE,{"disambiguationData":[OSD([sQuery(id+"F0.wireOp",EDGE,"E69.MirrorCS")])],"isStart":false});
            var Q17;
            Q17=makeQuery(id+"F2.opExtrude","CAP_EDGE",EDGE,{"disambiguationData":[OSD([sQuery(id+"F0.wireOp",EDGE,"E56.MirrorCS")])],"isStart":false});
            var Q18;
            Q18=makeQuery(id+"F2.opExtrude","CAP_EDGE",EDGE,{"disambiguationData":[OSD([sQuery(id+"F0.wireOp",EDGE,"E72.MirrorCS")])],"isStart":false});
            var Q19;
            Q19=makeQuery(id+"F2.opExtrude","CAP_EDGE",EDGE,{"disambiguationData":[OSD([sQuery(id+"F0.wireOp",EDGE,"E43.MirrorCS")])],"isStart":false});
            var Q20;
            Q20=makeQuery(id+"F2.opExtrude","CAP_EDGE",EDGE,{"disambiguationData":[OSD([sQuery(id+"F0.wireOp",EDGE,"E75")])],"isStart":false});
            var Q21;
            Q21=makeQuery(id+"F2.opExtrude","CAP_EDGE",EDGE,{"disambiguationData":[OSD([sQuery(id+"F0.wireOp",EDGE,"E22.MirrorCS")])],"isStart":false});
            var Q22;
            Q22=makeQuery(id+"F2.opExtrude","CAP_EDGE",EDGE,{"disambiguationData":[OSD([sQuery(id+"F0.wireOp",EDGE,"E33.MirrorCS")])],"isStart":false});
            var Q23;
            Q23=makeQuery(id+"F2.opExtrude","CAP_EDGE",EDGE,{"disambiguationData":[OSD([sQuery(id+"F0.wireOp",EDGE,"E28.MirrorCS")])],"isStart":false});
            var Q24;
            Q24=makeQuery(id+"F2.opExtrude","CAP_EDGE",EDGE,{"disambiguationData":[OSD([sQuery(id+"F0.wireOp",EDGE,"E31.MirrorCS")])],"isStart":false});
            var Q25;
            Q25=makeQuery(id+"F2.opExtrude","CAP_EDGE",EDGE,{"disambiguationData":[OSD([sQuery(id+"F0.wireOp",EDGE,"E25.MirrorCS")])],"isStart":false});
            var Q26;
            Q26=makeQuery(id+"F2.opExtrude","CAP_EDGE",EDGE,{"disambiguationData":[OSD([sQuery(id+"F0.wireOp",EDGE,"E40.MirrorCS")])],"isStart":false});
            var Q27;
            Q27=makeQuery(id+"F2.opExtrude","CAP_EDGE",EDGE,{"disambiguationData":[OSD([sQuery(id+"F0.wireOp",EDGE,"E21.MirrorCS")])],"isStart":false});
            var Q28;
            Q28=makeQuery(id+"F2.opExtrude","CAP_EDGE",EDGE,{"disambiguationData":[OSD([sQuery(id+"F0.wireOp",EDGE,"E37.MirrorCS")])],"isStart":false});
            var Q29;
            Q29=makeQuery(id+"F2.opExtrude","CAP_EDGE",EDGE,{"disambiguationData":[OSD([sQuery(id+"F0.wireOp",EDGE,"E35.MirrorCS")])],"isStart":false});
            var Q30;
            Q30=makeQuery(id+"F2.opExtrude","CAP_EDGE",EDGE,{"disambiguationData":[OSD([sQuery(id+"F0.wireOp",EDGE,"E34.MirrorCS")])],"isStart":false});
            var Q31;
            Q31=makeQuery(id+"F2.opExtrude","CAP_EDGE",EDGE,{"disambiguationData":[OSD([sQuery(id+"F0.wireOp",EDGE,"E26.MirrorCS")])],"isStart":false});
            var Q32;
            Q32=makeQuery(id+"F2.opExtrude","CAP_EDGE",EDGE,{"disambiguationData":[OSD([sQuery(id+"F0.wireOp",EDGE,"E23.MirrorCS")])],"isStart":false});
            var Q33;
            Q33=makeQuery(id+"F2.opExtrude","CAP_EDGE",EDGE,{"disambiguationData":[OSD([sQuery(id+"F0.wireOp",EDGE,"E32.MirrorCS")])],"isStart":false});
            var Q34;
            Q34=makeQuery(id+"F2.opExtrude","CAP_EDGE",EDGE,{"disambiguationData":[OSD([sQuery(id+"F0.wireOp",EDGE,"E29.MirrorCS")])],"isStart":false});
            var Q35;
            Q35=makeQuery(id+"F2.opExtrude","CAP_EDGE",EDGE,{"disambiguationData":[OSD([sQuery(id+"F0.wireOp",EDGE,"E27.MirrorCS")])],"isStart":false});
            var Q36;
            Q36=makeQuery(id+"F2.opExtrude","CAP_EDGE",EDGE,{"disambiguationData":[OSD([sQuery(id+"F0.wireOp",EDGE,"E30.MirrorCS")])],"isStart":false});
            var Q37;
            Q37=makeQuery(id+"F2.opExtrude","CAP_EDGE",EDGE,{"disambiguationData":[OSD([sQuery(id+"F0.wireOp",EDGE,"E5")])],"isStart":false});
            var Q38;
            Q38=makeQuery(id+"F2.opExtrude","CAP_EDGE",EDGE,{"disambiguationData":[OSD([sQuery(id+"F0.wireOp",EDGE,"E6")])],"isStart":false});
            var Q39;
            Q39=makeQuery(id+"F2.opExtrude","CAP_EDGE",EDGE,{"disambiguationData":[OSD([sQuery(id+"F0.wireOp",EDGE,"E7")])],"isStart":false});
            var Q40;
            Q40=makeQuery(id+"F2.opExtrude","CAP_EDGE",EDGE,{"disambiguationData":[OSD([sQuery(id+"F0.wireOp",EDGE,"E8")])],"isStart":false});
            var Q41;
            Q41=makeQuery(id+"F2.opExtrude","CAP_EDGE",EDGE,{"disambiguationData":[OSD([sQuery(id+"F0.wireOp",EDGE,"E9")])],"isStart":false});
            var Q42;
            Q42=makeQuery(id+"F2.opExtrude","CAP_EDGE",EDGE,{"disambiguationData":[OSD([sQuery(id+"F0.wireOp",EDGE,"E10")])],"isStart":false});
            var Q43;
            Q43=makeQuery(id+"F2.opExtrude","CAP_EDGE",EDGE,{"disambiguationData":[OSD([sQuery(id+"F0.wireOp",EDGE,"E11")])],"isStart":false});
            var Q44;
            Q44=makeQuery(id+"F2.opExtrude","CAP_EDGE",EDGE,{"disambiguationData":[OSD([sQuery(id+"F0.wireOp",EDGE,"E12")])],"isStart":false});
            var Q45;
            Q45=makeQuery(id+"F2.opExtrude","CAP_EDGE",EDGE,{"disambiguationData":[OSD([sQuery(id+"F0.wireOp",EDGE,"E13")])],"isStart":false});
            var Q46;
            Q46=makeQuery(id+"F2.opExtrude","CAP_EDGE",EDGE,{"disambiguationData":[OSD([sQuery(id+"F0.wireOp",EDGE,"E14")])],"isStart":false});
            var Q47;
            Q47=makeQuery(id+"F2.opExtrude","CAP_EDGE",EDGE,{"disambiguationData":[OSD([sQuery(id+"F0.wireOp",EDGE,"E15")])],"isStart":false});
            var Q48;
            Q48=makeQuery(id+"F2.opExtrude","CAP_EDGE",EDGE,{"disambiguationData":[OSD([sQuery(id+"F0.wireOp",EDGE,"E16")])],"isStart":false});
            var Q49;
            Q49=makeQuery(id+"F2.opExtrude","CAP_EDGE",EDGE,{"disambiguationData":[OSD([sQuery(id+"F0.wireOp",EDGE,"E17")])],"isStart":false});
            var Q50;
            Q50=makeQuery(id+"F2.opExtrude","CAP_EDGE",EDGE,{"disambiguationData":[OSD([sQuery(id+"F0.wireOp",EDGE,"E18")])],"isStart":false});
            var Q51;
            Q51=makeQuery(id+"F2.opExtrude","CAP_EDGE",EDGE,{"disambiguationData":[OSD([sQuery(id+"F0.wireOp",EDGE,"E19")])],"isStart":false});
            var Q52;
            Q52=makeQuery(id+"F2.opExtrude","CAP_EDGE",EDGE,{"disambiguationData":[OSD([sQuery(id+"F0.wireOp",EDGE,"E20")])],"isStart":false});
            var Q53;
            Q53=makeQuery(id+"F2.opExtrude","CAP_EDGE",EDGE,{"disambiguationData":[OSD([sQuery(id+"F0.wireOp",EDGE,"E74")])],"isStart":false});
            var Q54;
            Q54=makeQuery(id+"F2.opExtrude","CAP_EDGE",EDGE,{"disambiguationData":[OSD([sQuery(id+"F0.wireOp",EDGE,"E51.MirrorCS")])],"isStart":false});
            var Q55;
            Q55=makeQuery(id+"F2.opExtrude","CAP_EDGE",EDGE,{"disambiguationData":[OSD([sQuery(id+"F0.wireOp",EDGE,"E63.MirrorCS")])],"isStart":false});
            var Q56;
            Q56=makeQuery(id+"F2.opExtrude","CAP_EDGE",EDGE,{"disambiguationData":[OSD([sQuery(id+"F0.wireOp",EDGE,"E52.MirrorCS")])],"isStart":false});
            var Q57;
            Q57=makeQuery(id+"F2.opExtrude","CAP_EDGE",EDGE,{"disambiguationData":[OSD([sQuery(id+"F0.wireOp",EDGE,"E73.MirrorCS")])],"isStart":false});
            var Q58;
            Q58=makeQuery(id+"F2.opExtrude","CAP_EDGE",EDGE,{"disambiguationData":[OSD([sQuery(id+"F0.wireOp",EDGE,"E68.MirrorCS")])],"isStart":false});
            var Q59;
            Q59=makeQuery(id+"F2.opExtrude","CAP_EDGE",EDGE,{"disambiguationData":[OSD([sQuery(id+"F0.wireOp",EDGE,"E54.MirrorCS")])],"isStart":false});
            var Q60;
            Q60=makeQuery(id+"F2.opExtrude","CAP_EDGE",EDGE,{"disambiguationData":[OSD([sQuery(id+"F0.wireOp",EDGE,"E58.MirrorCS")])],"isStart":false});
            var Q61;
            Q61=makeQuery(id+"F2.opExtrude","CAP_EDGE",EDGE,{"disambiguationData":[OSD([sQuery(id+"F0.wireOp",EDGE,"E45.MirrorCS")])],"isStart":false});
            var Q62;
            Q62=makeQuery(id+"F2.opExtrude","CAP_EDGE",EDGE,{"disambiguationData":[OSD([sQuery(id+"F0.wireOp",EDGE,"E61.MirrorCS")])],"isStart":false});
            var Q63;
            Q63=makeQuery(id+"F2.opExtrude","CAP_EDGE",EDGE,{"disambiguationData":[OSD([sQuery(id+"F0.wireOp",EDGE,"E49.MirrorCS")])],"isStart":false});
            chamfer(context, id + "F4", {"entities" : qUnion([Q0, Q1, Q2, Q3, Q4, Q5, Q6, Q7, Q8, Q9, Q10, Q11, Q12, Q13, Q14, Q15, Q16, Q17, Q18, Q19, Q20, Q21, Q22, Q23, Q24, Q25, Q26, Q27, Q28, Q29, Q30, Q31, Q32, Q33, Q34, Q35, Q36, Q37, Q38, Q39, Q40, Q41, Q42, Q43, Q44, Q45, Q46, Q47, Q48, Q49, Q50, Q51, Q52, Q53, Q54, Q55, Q56, Q57, Q58, Q59, Q60, Q61, Q62, Q63]), "width" : 0.5 * mm, "tangentPropagation" : true});
        }
        {
            var Q0;
            Q0=sQuery(id+"F0.wireOp",VERTEX,"E0.cCircle.center");
            var Q1;
            Q1=makeQuery(id+"F1.opExtrude","SWEPT_BODY",BODY,{"disambiguationData":[OSD([sQuery(id+"F0.wireOp",EDGE,"E5"),sQuery(id+"F0.wireOp",EDGE,"E6"),sQuery(id+"F0.wireOp",EDGE,"E7"),sQuery(id+"F0.wireOp",EDGE,"E8"),sQuery(id+"F0.wireOp",EDGE,"E9"),sQuery(id+"F0.wireOp",EDGE,"E10"),sQuery(id+"F0.wireOp",EDGE,"E11"),sQuery(id+"F0.wireOp",EDGE,"E12"),sQuery(id+"F0.wireOp",EDGE,"E13"),sQuery(id+"F0.wireOp",EDGE,"E14"),sQuery(id+"F0.wireOp",EDGE,"E15"),sQuery(id+"F0.wireOp",EDGE,"E16"),sQuery(id+"F0.wireOp",EDGE,"E17"),sQuery(id+"F0.wireOp",EDGE,"E18"),sQuery(id+"F0.wireOp",EDGE,"E19"),sQuery(id+"F0.wireOp",EDGE,"E20"),sQuery(id+"F0.wireOp",EDGE,"E21.MirrorCS"),sQuery(id+"F0.wireOp",EDGE,"E22.MirrorCS"),sQuery(id+"F0.wireOp",EDGE,"E23.MirrorCS"),sQuery(id+"F0.wireOp",EDGE,"E25.MirrorCS"),sQuery(id+"F0.wireOp",EDGE,"E26.MirrorCS"),sQuery(id+"F0.wireOp",EDGE,"E27.MirrorCS"),sQuery(id+"F0.wireOp",EDGE,"E28.MirrorCS"),sQuery(id+"F0.wireOp",EDGE,"E29.MirrorCS"),sQuery(id+"F0.wireOp",EDGE,"E30.MirrorCS"),sQuery(id+"F0.wireOp",EDGE,"E31.MirrorCS"),sQuery(id+"F0.wireOp",EDGE,"E32.MirrorCS"),sQuery(id+"F0.wireOp",EDGE,"E33.MirrorCS"),sQuery(id+"F0.wireOp",EDGE,"E34.MirrorCS"),sQuery(id+"F0.wireOp",EDGE,"E35.MirrorCS"),sQuery(id+"F0.wireOp",EDGE,"E37.MirrorCS"),sQuery(id+"F0.wireOp",EDGE,"E40.MirrorCS"),sQuery(id+"F0.wireOp",EDGE,"E42.MirrorCS"),sQuery(id+"F0.wireOp",EDGE,"E43.MirrorCS"),sQuery(id+"F0.wireOp",EDGE,"E44.MirrorCS"),sQuery(id+"F0.wireOp",EDGE,"E45.MirrorCS"),sQuery(id+"F0.wireOp",EDGE,"E46.MirrorCS"),sQuery(id+"F0.wireOp",EDGE,"E47.MirrorCS"),sQuery(id+"F0.wireOp",EDGE,"E48.MirrorCS"),sQuery(id+"F0.wireOp",EDGE,"E49.MirrorCS"),sQuery(id+"F0.wireOp",EDGE,"E50.MirrorCS"),sQuery(id+"F0.wireOp",EDGE,"E51.MirrorCS"),sQuery(id+"F0.wireOp",EDGE,"E52.MirrorCS"),sQuery(id+"F0.wireOp",EDGE,"E53.MirrorCS"),sQuery(id+"F0.wireOp",EDGE,"E54.MirrorCS"),sQuery(id+"F0.wireOp",EDGE,"E55.MirrorCS"),sQuery(id+"F0.wireOp",EDGE,"E56.MirrorCS"),sQuery(id+"F0.wireOp",EDGE,"E57.MirrorCS"),sQuery(id+"F0.wireOp",EDGE,"E58.MirrorCS"),sQuery(id+"F0.wireOp",EDGE,"E60.MirrorCS"),sQuery(id+"F0.wireOp",EDGE,"E61.MirrorCS"),sQuery(id+"F0.wireOp",EDGE,"E62.MirrorCS"),sQuery(id+"F0.wireOp",EDGE,"E63.MirrorCS"),sQuery(id+"F0.wireOp",EDGE,"E64.MirrorCS"),sQuery(id+"F0.wireOp",EDGE,"E66.MirrorCS"),sQuery(id+"F0.wireOp",EDGE,"E67.MirrorCS"),sQuery(id+"F0.wireOp",EDGE,"E68.MirrorCS"),sQuery(id+"F0.wireOp",EDGE,"E69.MirrorCS"),sQuery(id+"F0.wireOp",EDGE,"E70.MirrorCS"),sQuery(id+"F0.wireOp",EDGE,"E71.MirrorCS"),sQuery(id+"F0.wireOp",EDGE,"E72.MirrorCS"),sQuery(id+"F0.wireOp",EDGE,"E73.MirrorCS"),sQuery(id+"F0.wireOp",EDGE,"E74"),sQuery(id+"F0.wireOp",EDGE,"E75")])]});
            hole(context, id + "F5", {"style" : HoleStyle.SIMPLE, "endStyle" : HoleEndStyle.BLIND, "oppositeDirection" : true, "holeDiameter" : 8 * mm, "majorDiameter" : 5 * mm, "holeDepth" : 8 * mm, "isTappedThrough" : true, "tappedDepth" : 12 * mm, "tapClearance" : 3, "startFromSketch" : true, "locations" : qUnion([Q0]), "scope" : qUnion([Q1])});
        }
    });
